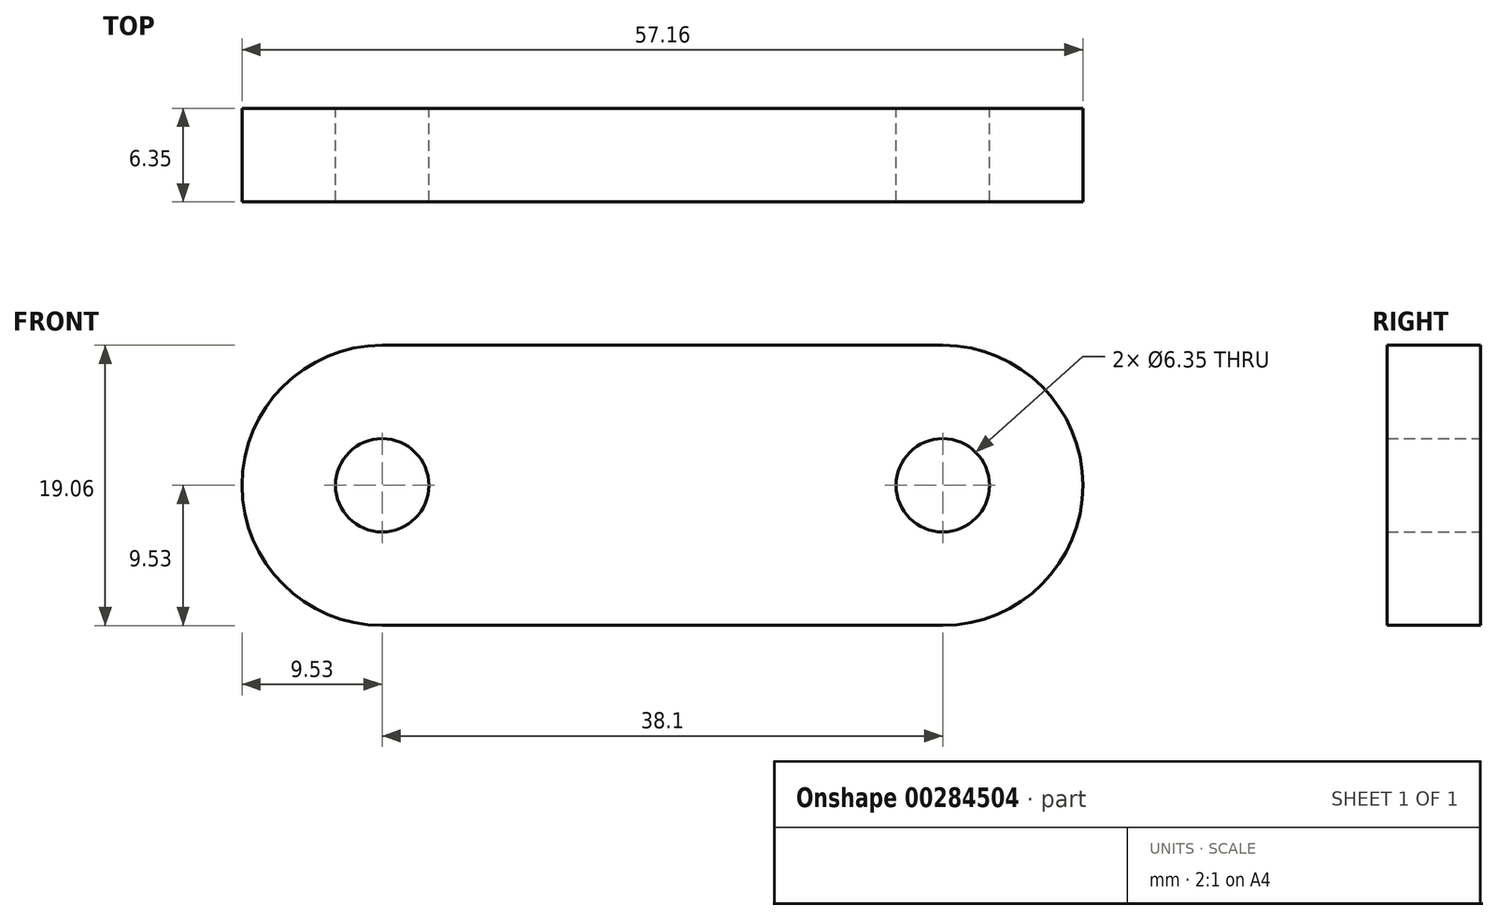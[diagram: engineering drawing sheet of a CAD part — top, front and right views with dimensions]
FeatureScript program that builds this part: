
annotation { "Feature Type Name" : "Feature", "Feature Type Description" : "" }
export const myFeature = defineFeature(function(context is Context, id is Id, definition is map)
    precondition{}
    {
        {
            var Q0;
            Q0=qCreatedBy(makeId("Front.planeOp"),FACE);
            var sketch = newSketch(context, id + "F0", { "sketchPlane" : qUnion([Q0])});
            skLineSegment(sketch, "E0.bottom", {"start": v(-19.05, 9.53) * mm, "end": v(19.05, 9.53) * mm});
            skLineSegment(sketch, "E0.top", {"start": v(-19.05, -9.52) * mm, "end": v(19.05, -9.52) * mm});
            skPoint(sketch, "E0.middle", {"position": v(0, 0) * mm});
            skArc(sketch, "E1", {"start": v(-19.05, 9.53) * mm, "mid": v(-28.58, 0) * mm, "end": v(-19.05, -9.53) * mm});
            skArc(sketch, "E2", {"start": v(19.05, -9.53) * mm, "mid": v(28.58, 0) * mm, "end": v(19.05, 9.53) * mm});
            skCircle(sketch, "E3", {"center": v(-19.05, 0) * mm, "radius": 3.18 * mm});
            skCircle(sketch, "E4", {"center": v(19.05, 0) * mm, "radius": 3.18 * mm});
            skLineSegment(sketch, "E5", {"start": v(-19.05, 9.53) * mm, "end": v(-19.05, -9.52) * mm});
            skSolve(sketch);
        }
        {
            var Q0;
            {var subQ5=sQuery(id+"F0.wireOp",EDGE,"E0.bottom");Q0=makeQuery(id+"F0.imprint","IMPRINT",FACE,{"disambiguationData":[TD([[makeQuery(id+"F0.imprint","IMPRINT",EDGE,{"derivedFrom":subQ5}),-1.0]])]});}
            var Q1;
            {var subQ0=sQuery(id+"F0.wireOp",EDGE,"E1");Q1=makeQuery(id+"F0.imprint","IMPRINT",FACE,{"disambiguationData":[TD([[makeQuery(id+"F0.imprint","IMPRINT",EDGE,{"derivedFrom":subQ0}),1.0]])]});}
            extrude(context, id + "F1", {"entities" : qUnion([Q0, Q1]), "depth" : 6.35 * mm});
        }
    });
